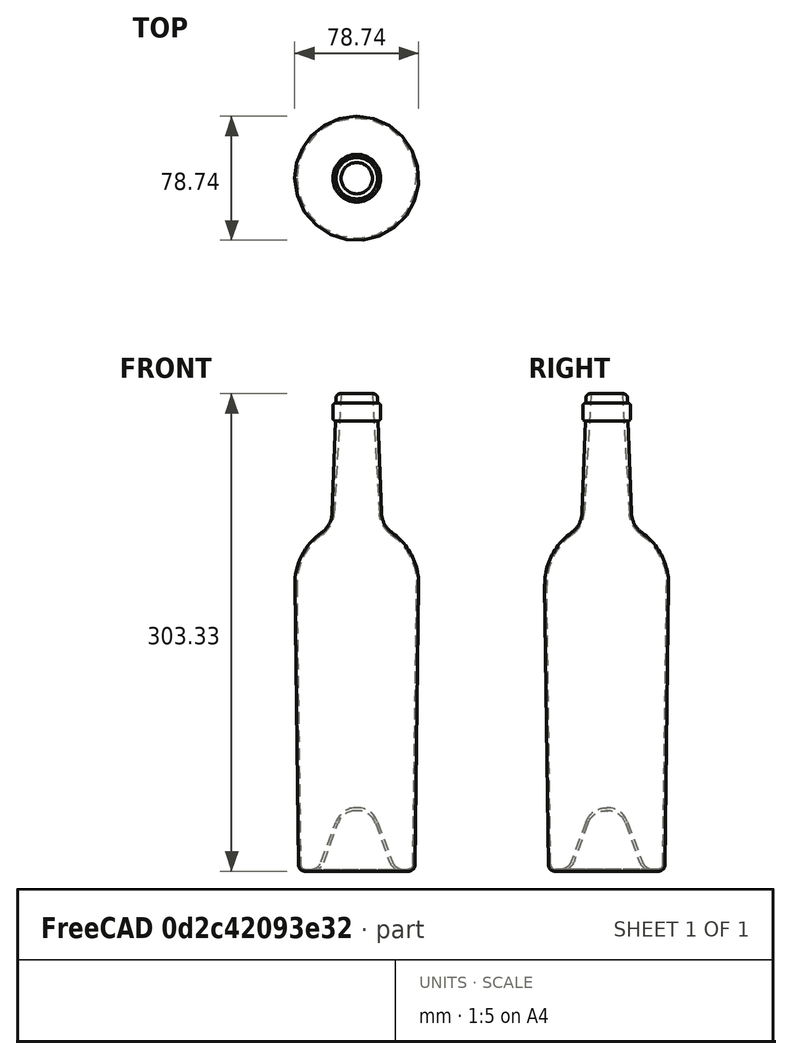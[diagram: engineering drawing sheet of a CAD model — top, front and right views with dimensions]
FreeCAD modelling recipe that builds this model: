
FCSTD DOCUMENT  (FreeCAD 0.20R24789 (Git))
Label: 217 - BOTTLE
License: Creative Commons Attribution-NonCommercial
LicenseURL: http://creativecommons.org/licenses/by-nc/4.0/
objects: Sketcher::SketchObject×2, Image::ImagePlane×1, PartDesign::Revolution×1, PartDesign::Groove×1, PartDesign::Body×1
note: 7 computed .brp shape members not serialized (recipe doc carries the construction recipe); baked Part::Feature solids carry a one-line shape summary decoded from their .brp

FEATURE [Image::ImagePlane] ImagePlane
  Placement = pos=(-59,0,-29) rot=(-1,0,0;4.71239rad)
  XSize = 296.385
  YSize = 337.905
FEATURE [Sketcher::SketchObject] Sketch
  FullyConstrained = false
  MapMode = 5
  Placement = pos=(0,0,0) rot=(1,0,0;1.5708rad)
  Support = -> [XZ_Plane]
  sketch-geometry (16):
    g0: LineSegment StartX=0 StartY=121.755 StartZ=0 EndX=-10.5579 EndY=121.755 EndZ=0
    g1: ArcOfCircle CenterX=-10.5579 CenterY=119.189 CenterZ=0 NormalX=0 NormalY=0 NormalZ=1 AngleXU=0 Radius=2.56629 StartAngle=1.5708 EndAngle=3.14159
    g2: LineSegment StartX=-13.1242 StartY=119.189 StartZ=0 EndX=-13.1242 EndY=115.89 EndZ=0
    g3: ArcOfCircle CenterX=-13.1242 CenterY=113.837 CenterZ=0 NormalX=0 NormalY=0 NormalZ=1 AngleXU=0 Radius=2.05296 StartAngle=1.5708 EndAngle=3.14159
    g4: LineSegment StartX=-15.1771 StartY=113.837 StartZ=0 EndX=-15.1771 EndY=106.2 EndZ=0
    g5: ArcOfCircle CenterX=-13.4908 CenterY=106.2 CenterZ=0 NormalX=0 NormalY=0 NormalZ=1 AngleXU=0 Radius=1.68635 StartAngle=3.14159 EndAngle=4.67686
    g6: LineSegment StartX=-13.5507 StartY=104.515 StartZ=0 EndX=-15.623 EndY=46.2103 EndZ=0
    g7: ArcOfCircle CenterX=-31.9614 CenterY=46.7911 CenterZ=0 NormalX=0 NormalY=0 NormalZ=1 AngleXU=0 Radius=16.3487 StartAngle=5.33417 EndAngle=6.24766
    g8: ArcOfCircle CenterX=1.1835 CenterY=0.53846 CenterZ=0 NormalX=0 NormalY=0 NormalZ=1 AngleXU=0 Radius=40.5537 StartAngle=2.19258 EndAngle=3.15487
    g9: LineSegment StartX=-39.3666 StartY=-1.3e-15 StartZ=0 EndX=-37.0098 EndY=-177.49 EndZ=0
    g10: ArcOfCircle CenterX=-32.8769 CenterY=-177.435 CenterZ=0 NormalX=0 NormalY=0 NormalZ=1 AngleXU=0 Radius=4.13324 StartAngle=3.15487 EndAngle=4.71239
    g11: LineSegment StartX=-32.8769 StartY=-181.569 StartZ=0 EndX=-29.1748 EndY=-181.569 EndZ=0
    g12: ArcOfCircle CenterX=-29.1748 CenterY=-172.79 CenterZ=0 NormalX=0 NormalY=0 NormalZ=1 AngleXU=0 Radius=8.77854 StartAngle=4.71239 EndAngle=5.93207
    g13: LineSegment StartX=-20.9319 StartY=-175.81 StartZ=0 EndX=-11.7766 EndY=-150.815 EndZ=0
    g14: ArcOfCircle CenterX=-0.875952 CenterY=-154.808 CenterZ=0 NormalX=0 NormalY=0 NormalZ=1 AngleXU=0 Radius=11.6089 StartAngle=1.49527 EndAngle=2.79048
    g15: LineSegment StartX=-1e-16 StartY=-143.232 StartZ=0 EndX=0 EndY=121.755 EndZ=0
  constraints (23):
    c: PointOnObject(g0,g-2)
    c: Horizontal(g0)
    c: Tangent(g0,g1) = -1.5708
    c: Tangent(g1,g2) = -1.5708
    c: Vertical(g2)
    c: Perpendicular(g2,g3) = 4.71239
    c: Tangent(g3,g4) = -1.5708
    c: Vertical(g4)
    c: Tangent(g4,g5) = -1.5708
    c: Perpendicular(g5,g6) = 4.71239
    c: Tangent(g6,g7) = 1.5708
    c: Tangent(g7,g8) = 1.5708
    c: PointOnObject(g8,g-1)
    c: Tangent(g8,g9) = -1.5708
    c: Tangent(g9,g10) = -1.5708
    c: Tangent(g10,g11) = -1.5708
    c: Horizontal(g11)
    c: Tangent(g11,g12) = -1.5708
    c: Tangent(g12,g13) = -1.5708
    c: Tangent(g13,g14) = 1.5708
    c: PointOnObject(g14,g-2)
    c: Coincident(g14,g15)
    c: Coincident(g15,g0)
FEATURE [Sketcher::SketchObject] Sketch001
  ExternalGeometry = -> [Sketch]
  FullyConstrained = false
  MapMode = 5
  Placement = pos=(0,0,0) rot=(1,0,0;1.5708rad)
  Support = -> [XZ_Plane]
  sketch-geometry (11):
    g0: LineSegment StartX=0 StartY=123.123 StartZ=0 EndX=-9.86221 EndY=123.123 EndZ=0
    g1: LineSegment StartX=-9.86221 StartY=123.123 StartZ=0 EndX=-14.3625 EndY=45.7672 EndZ=0
    g2: ArcOfCircle CenterX=-31.9614 CenterY=46.7911 CenterZ=0 NormalX=0 NormalY=0 NormalZ=1 AngleXU=0 Radius=17.6287 StartAngle=5.33417 EndAngle=6.22507
    g3: ArcOfCircle CenterX=1.1835 CenterY=0.53846 CenterZ=0 NormalX=0 NormalY=0 NormalZ=1 AngleXU=0 Radius=39.2738 StartAngle=2.19258 EndAngle=3.1553
    g4: LineSegment StartX=-38.0866 StartY=-8.1e-15 StartZ=0 EndX=-35.6562 EndY=-177.248 EndZ=0
    g5: ArcOfCircle CenterX=-32.5088 CenterY=-177.205 CenterZ=0 NormalX=0 NormalY=0 NormalZ=1 AngleXU=0 Radius=3.1477 StartAngle=3.1553 EndAngle=4.71239
    g6: LineSegment StartX=-32.5088 StartY=-180.352 StartZ=0 EndX=-29.415 EndY=-180.352 EndZ=0
    g7: ArcOfCircle CenterX=-29.415 CenterY=-173.109 CenterZ=0 NormalX=0 NormalY=0 NormalZ=1 AngleXU=0 Radius=7.24301 StartAngle=4.71239 EndAngle=5.92838
    g8: LineSegment StartX=-22.6231 StartY=-175.626 StartZ=0 EndX=-13.198 EndY=-150.186 EndZ=0
    g9: ArcOfCircle CenterX=-0.282362 CenterY=-154.971 CenterZ=0 NormalX=0 NormalY=0 NormalZ=1 AngleXU=0 Radius=13.7735 StartAngle=1.55029 EndAngle=2.78678
    g10: LineSegment StartX=-6e-16 StartY=-141.2 StartZ=0 EndX=0 EndY=123.123 EndZ=0
  constraints (20):
    c: PointOnObject(g0,g-2)
    c: Coincident(g0,g1)
    c: Horizontal(g0)
    c: Tangent(g1,g2) = 1.5708
    c: Tangent(g2,g3) = 1.5708
    c: PointOnObject(g3,g-1)
    c: Tangent(g3,g4) = -1.5708
    c: Coincident(g3,g-4)
    c: Coincident(g-3,g2)
    c: DistanceX(g0) = -9.86221
    c: DistanceY(g0) = 123.123
    c: Tangent(g4,g5) = -1.5708
    c: Tangent(g5,g6) = -1.5708
    c: Tangent(g6,g7) = -1.5708
    c: Tangent(g7,g8) = -1.5708
    c: Tangent(g8,g9) = 1.5708
    c: PointOnObject(g9,g-2)
    c: Coincident(g9,g10)
    c: Coincident(g0,g10)
    c: Horizontal(g6)
FEATURE [PartDesign::Revolution] Revolution
  Angle = 360
  Axis = (0,2e-16,1)
  Base = (0,0,0)
  Placement = pos=(0,0,0) rot=(1,0,0;1.5708rad)
  Profile = -> Sketch
  ReferenceAxis = -> Sketch [V_Axis]
FEATURE [PartDesign::Groove] Groove
  Angle = 360
  Axis = (0,2e-16,1)
  Base = (0,0,0)
  BaseFeature = -> Revolution
  Placement = pos=(0,0,0) rot=(1,0,0;1.5708rad)
  Profile = -> Sketch001
  ReferenceAxis = -> Sketch001 [V_Axis]
  Reversed = true
FEATURE [PartDesign::Body] Body
  Group = -> [Sketch,Sketch001,Revolution,Groove]
  Origin = -> Origin
  Tip = -> Groove
